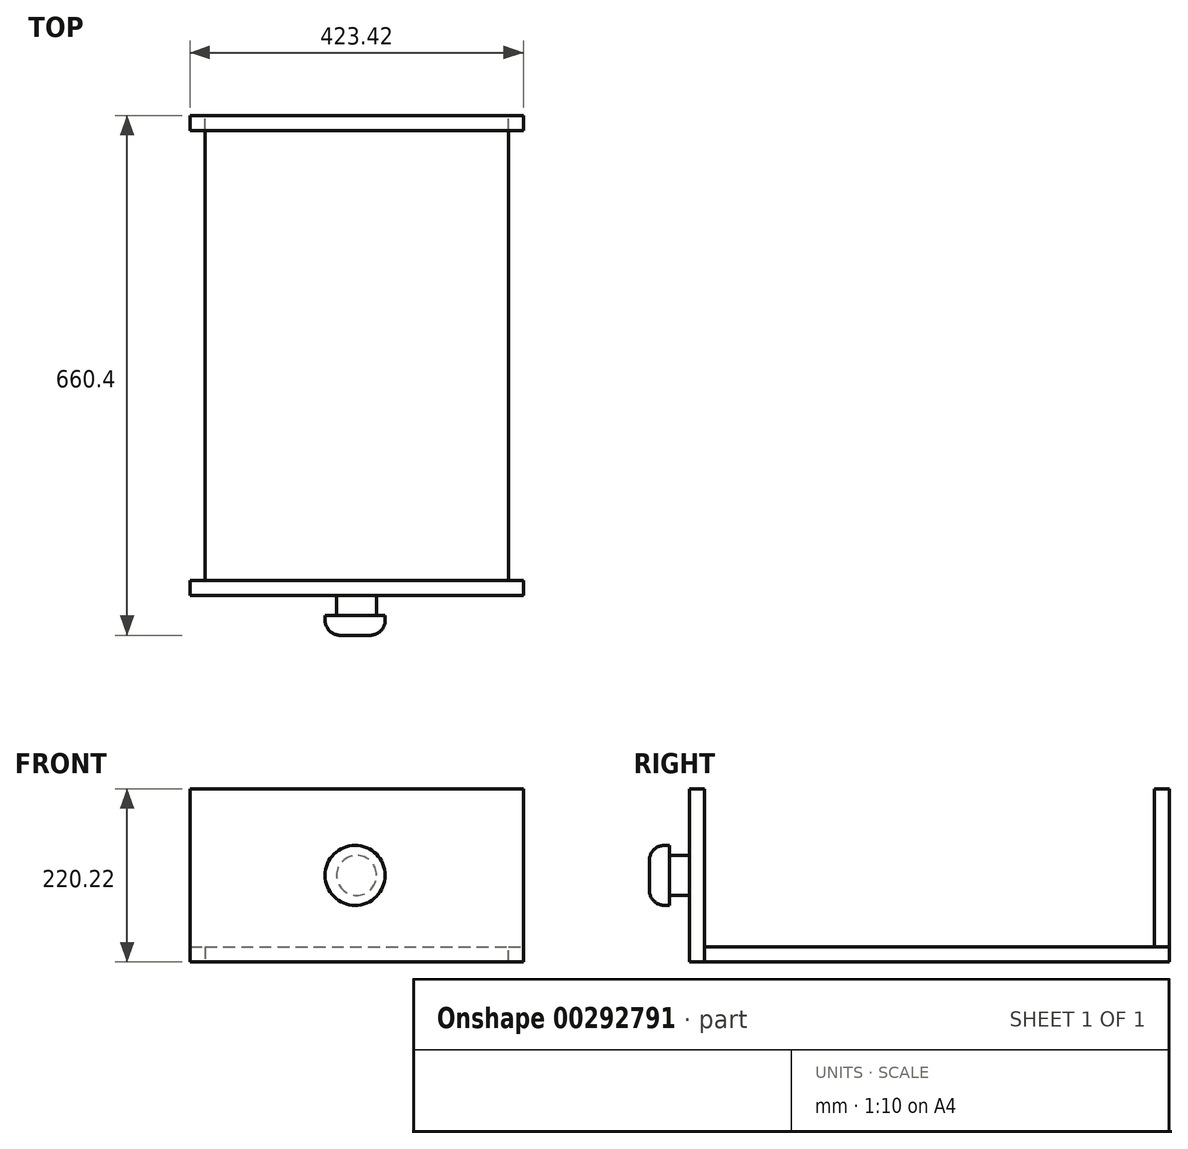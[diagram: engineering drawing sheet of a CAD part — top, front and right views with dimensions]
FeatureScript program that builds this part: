
annotation { "Feature Type Name" : "Feature", "Feature Type Description" : "" }
export const myFeature = defineFeature(function(context is Context, id is Id, definition is map)
    precondition{}
    {
        {
            var Q0;
            Q0=qCreatedBy(makeId("Front.planeOp"),FACE);
            var sketch = newSketch(context, id + "F0", { "sketchPlane" : qUnion([Q0])});
            skLineSegment(sketch, "E0.bottom", {"start": v(-209.62, -73.9) * mm, "end": v(213.8, -73.9) * mm});
            skLineSegment(sketch, "E0.top", {"start": v(-209.62, 146.3) * mm, "end": v(213.8, 146.3) * mm});
            skLineSegment(sketch, "E0.left", {"start": v(-209.62, -73.9) * mm, "end": v(-209.62, 146.3) * mm});
            skLineSegment(sketch, "E0.right", {"start": v(213.8, -73.9) * mm, "end": v(213.8, 146.3) * mm});
            skLineSegment(sketch, "E1.bottom", {"start": v(-209.62, 146.3) * mm, "end": v(-190.57, 146.3) * mm});
            skLineSegment(sketch, "E1.top", {"start": v(-209.62, -73.9) * mm, "end": v(-190.57, -73.9) * mm});
            skLineSegment(sketch, "E1.left", {"start": v(-209.62, 146.3) * mm, "end": v(-209.62, -73.9) * mm});
            skLineSegment(sketch, "E1.right", {"start": v(-190.57, 146.3) * mm, "end": v(-190.57, -73.9) * mm});
            skLineSegment(sketch, "E2.top", {"start": v(-209.62, -54.86) * mm, "end": v(213.8, -54.86) * mm});
            skLineSegment(sketch, "E2.left", {"start": v(-209.62, -73.9) * mm, "end": v(-209.62, -54.86) * mm});
            skLineSegment(sketch, "E2.right", {"start": v(213.8, -73.9) * mm, "end": v(213.8, -54.86) * mm});
            skLineSegment(sketch, "E3.bottom", {"start": v(213.8, -73.9) * mm, "end": v(194.75, -73.9) * mm});
            skLineSegment(sketch, "E3.top", {"start": v(213.8, 146.3) * mm, "end": v(194.75, 146.3) * mm});
            skLineSegment(sketch, "E3.right", {"start": v(194.75, -73.9) * mm, "end": v(194.75, 146.3) * mm});
            skSolve(sketch);
        }
        {
            var Q0;
            {var subQ0=sQuery(id+"F0.wireOp",EDGE,"E0.top");Q0=makeQuery(id+"F0.imprint","IMPRINT",FACE,{"disambiguationData":[TD([[makeQuery(id+"F0.imprint","IMPRINT",EDGE,{"derivedFrom":subQ0}),-1.0]])]});}
            extrude(context, id + "F1", {"entities" : qUnion([Q0]), "depth" : 19.05 * mm});
        }
        {
            var Q0;
            {var subQ5=sQuery(id+"F0.wireOp",EDGE,"E3.top");Q0=makeQuery(id+"F0.imprint","IMPRINT",FACE,{"disambiguationData":[TD([[makeQuery(id+"F0.imprint","IMPRINT",EDGE,{"derivedFrom":subQ5}),1.0]])]});}
            var Q1;
            {var subQ0=sQuery(id+"F0.wireOp",EDGE,"E1.bottom");Q1=makeQuery(id+"F0.imprint","IMPRINT",FACE,{"disambiguationData":[TD([[makeQuery(id+"F0.imprint","IMPRINT",EDGE,{"derivedFrom":subQ0}),-1.0]])]});}
            var Q2;
            {var subQ0=sQuery(id+"F0.wireOp",EDGE,"E0.bottom");var subQ1=sQuery(id+"F0.wireOp",EDGE,"E1.right");var subQ2=makeQuery(id+"F0.imprint","INTERSECT",VERTEX,{"derivedFrom":[subQ1,subQ0]});Q2=makeQuery(id+"F0.imprint","IMPRINT",FACE,{"disambiguationData":[TD([[makeQuery(id+"F0.imprint","IMPRINT",EDGE,{"disambiguationData":[TD([[subQ2,1.0]])],"derivedFrom":subQ1}),1.0]])]});}
            var Q3;
            {var subQ5=sQuery(id+"F0.wireOp",EDGE,"E2.left");Q3=makeQuery(id+"F0.imprint","IMPRINT",FACE,{"disambiguationData":[TD([[makeQuery(id+"F0.imprint","IMPRINT",EDGE,{"derivedFrom":subQ5}),-1.0]])]});}
            var Q4;
            {var subQ5=sQuery(id+"F0.wireOp",EDGE,"E3.bottom");Q4=makeQuery(id+"F0.imprint","IMPRINT",FACE,{"disambiguationData":[TD([[makeQuery(id+"F0.imprint","IMPRINT",EDGE,{"derivedFrom":subQ5}),-1.0]])]});}
            extrude(context, id + "F2", {"entities" : qUnion([Q0, Q1, Q2, Q3, Q4]), "operationType" : NewBodyOperationType.ADD, "depth" : 590.55 * mm});
        }
        {
            var Q0;
            Q0=makeQuery(id+"F2.opExtrude","CAP_FACE",FACE,{"disambiguationData":[OSD([sQuery(id+"F0.wireOp",EDGE,"E1.bottom"),sQuery(id+"F0.wireOp",EDGE,"E1.left"),sQuery(id+"F0.wireOp",EDGE,"E1.right"),sQuery(id+"F0.wireOp",EDGE,"E0.bottom"),sQuery(id+"F0.wireOp",EDGE,"E2.top"),sQuery(id+"F0.wireOp",EDGE,"E2.left"),sQuery(id+"F0.wireOp",EDGE,"E3.bottom"),sQuery(id+"F0.wireOp",EDGE,"E3.top"),sQuery(id+"F0.wireOp",EDGE,"E0.right"),sQuery(id+"F0.wireOp",EDGE,"E3.right")])],"isStart":false});
            var sketch = newSketch(context, id + "F3", { "sketchPlane" : qUnion([Q0])});
            skLineSegment(sketch, "E4.bottom", {"start": v(-209.62, -73.9) * mm, "end": v(213.8, -73.9) * mm});
            skLineSegment(sketch, "E4.top", {"start": v(-209.62, 146.3) * mm, "end": v(213.8, 146.3) * mm});
            skLineSegment(sketch, "E4.left", {"start": v(-209.62, -73.9) * mm, "end": v(-209.62, 146.3) * mm});
            skLineSegment(sketch, "E4.right", {"start": v(213.8, -73.9) * mm, "end": v(213.8, 146.3) * mm});
            skSolve(sketch);
        }
        {
            var Q0;
            Q0 = qSketchRegion(id + "F3", true);
            extrude(context, id + "F4", {"entities" : qUnion([Q0]), "operationType" : NewBodyOperationType.ADD, "depth" : 19.05 * mm});
        }
        {
            var Q0;
            Q0=makeQuery(id+"F4.opExtrude","CAP_FACE",FACE,{"disambiguationData":[OSD([sQuery(id+"F3.wireOp",EDGE,"E4.bottom"),sQuery(id+"F3.wireOp",EDGE,"E4.top"),sQuery(id+"F3.wireOp",EDGE,"E4.left"),sQuery(id+"F3.wireOp",EDGE,"E4.right")])],"isStart":false});
            var sketch = newSketch(context, id + "F5", { "sketchPlane" : qUnion([Q0])});
            skCircle(sketch, "E5", {"center": v(1.96, 36.33) * mm, "radius": 25.4 * mm});
            skCircle(sketch, "E6.0", {"center": v(1.96, 36.33) * mm, "radius": 44.45 * mm});
            skSolve(sketch);
        }
        {
            var Q0;
            Q0=makeQuery(id+"F5.imprint","IMPRINT",FACE,{"disambiguationData":[TD([[makeQuery(id+"F5.imprint","IMPRINT",EDGE,{"derivedFrom":sQuery(id+"F5.wireOp",EDGE,"E5")}),1.0]])]});
            extrude(context, id + "F6", {"entities" : qUnion([Q0]), "operationType" : NewBodyOperationType.ADD, "depth" : 25.4 * mm});
        }
        {
            var Q0;
            Q0=makeQuery(id+"F6.opExtrude","CAP_FACE",FACE,{"disambiguationData":[OSD([sQuery(id+"F5.wireOp",EDGE,"E5")])],"isStart":false});
            var sketch = newSketch(context, id + "F7", { "sketchPlane" : qUnion([Q0])});
            skSolve(sketch);
        }
        {
            var Q0;
            Q0=makeQuery(id+"F7.imprint","IMPRINT",FACE,{"disambiguationData":[TD([[makeQuery(id+"F7.imprint","IMPRINT",EDGE,{"derivedFrom":makeQuery(id+"F6.opExtrude","CAP_EDGE",EDGE,{"disambiguationData":[OSD([sQuery(id+"F5.wireOp",EDGE,"E5")])],"isStart":false})}),1.0]])]});
            var sketch = newSketch(context, id + "F8", { "sketchPlane" : qUnion([Q0])});
            skCircle(sketch, "E7", {"center": v(0, 36.33) * mm, "radius": 38.1 * mm});
            skSolve(sketch);
        }
        {
            var Q0;
            Q0 = qSketchRegion(id + "F8", true);
            extrude(context, id + "F9", {"entities" : qUnion([Q0]), "operationType" : NewBodyOperationType.ADD, "depth" : 25.4 * mm});
        }
        {
            var Q0;
            Q0=makeQuery(id+"F9.opExtrude","CAP_EDGE",EDGE,{"disambiguationData":[OSD([sQuery(id+"F8.wireOp",EDGE,"E7")])],"isStart":false});
            fillet(context, id + "F10", {"entities" : qUnion([Q0]), "radius" : 19.05 * mm, "tangentPropagation" : true, "allowEdgeOverflow" : false});
        }
    });
